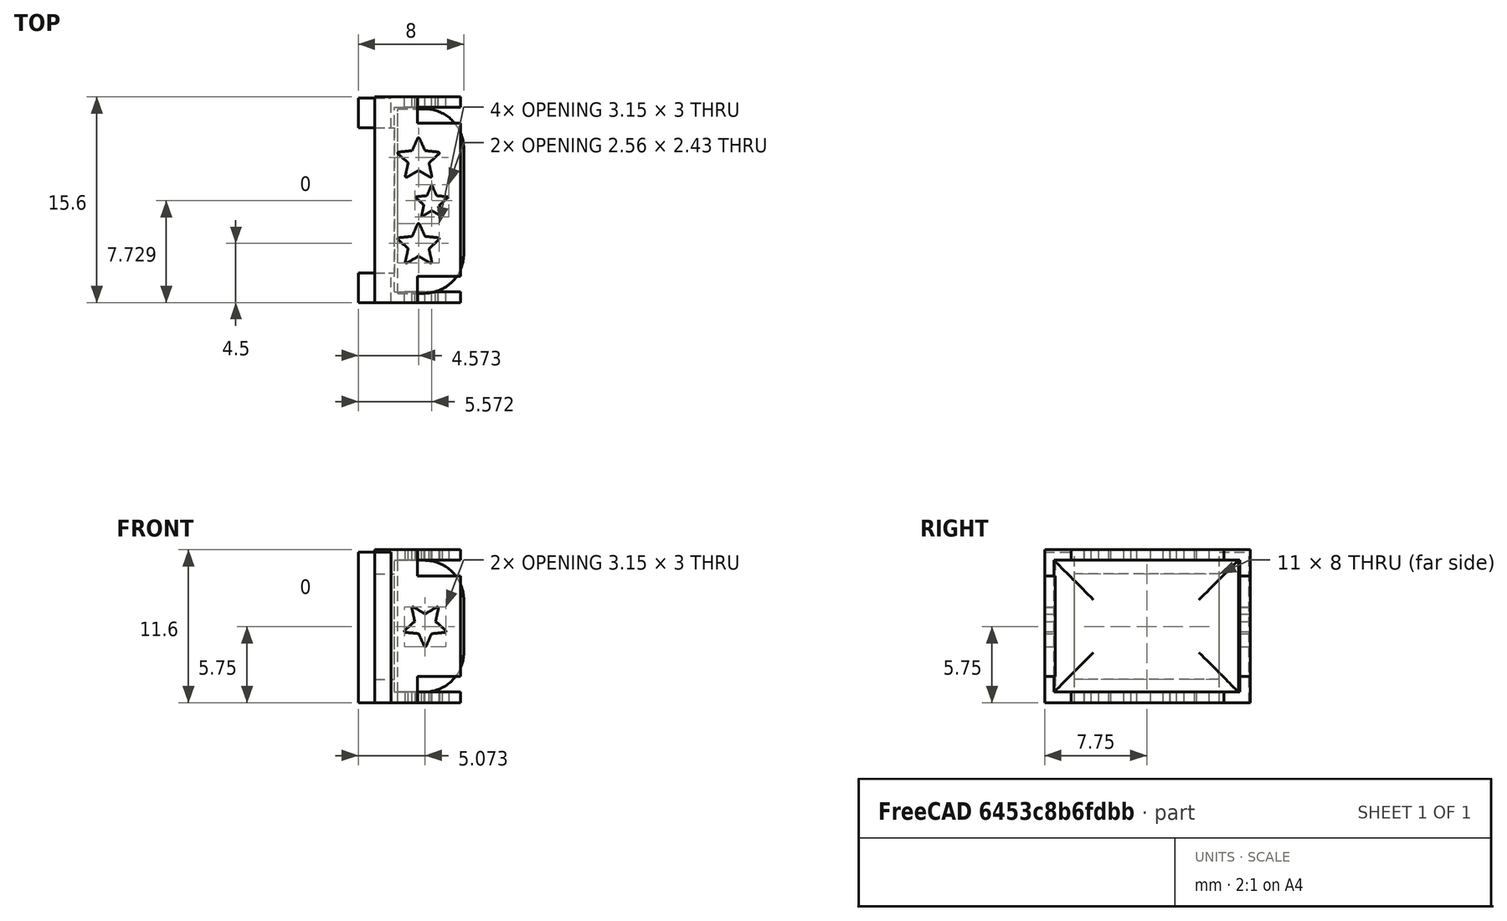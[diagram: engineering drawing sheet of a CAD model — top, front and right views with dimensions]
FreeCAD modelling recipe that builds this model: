
FCSTD DOCUMENT  (FreeCAD 0.19R)
Label: 14mmx10mm_rectangle_cabuchon
License: All rights reserved
LicenseURL: http://en.wikipedia.org/wiki/All_rights_reserved
objects: Part::Cut×11, Part::Box×10, Part::Feature×5, Part::Extrusion×5, Part::Fillet×1
note: 32 computed .brp shape members not serialized (recipe doc carries the construction recipe); baked Part::Feature solids carry a one-line shape summary decoded from their .brp

FEATURE [Part::Box] Box  label="Cube"
  AttacherType = Attacher::AttachEngine3D
  Height = 11.6
  Length = 6.5
  Placement = pos=(10.5,-7.5,-6.5) rot=(0,0,1;0rad)
  Width = 15.6
FEATURE [Part::Box] Box002  label="Cube002"
  AttacherType = Attacher::AttachEngine3D
  Height = 10
  Length = 5.75
  Placement = pos=(12,-6.7,-5.7) rot=(0,0,1;0rad)
  Width = 14
FEATURE [Part::Cut] Cut
  Base = -> Box
  Placement = pos=(1,0,0) rot=(0,0,1;0rad)
  Tool = -> Box002
FEATURE [Part::Box] Box004  label="Cube004"
  AttacherType = Attacher::AttachEngine3D
  Height = 8
  Length = 8
  Placement = pos=(11,-5.25,-4.75) rot=(0,0,1;0rad)
  Width = 11
FEATURE [Part::Cut] Cut001
  Base = -> Cut
  Placement = pos=(-1.25,0,0) rot=(0,0,1;0rad)
  Tool = -> Box004
FEATURE [Part::Box] Box006  label="Cube006"
  AttacherType = Attacher::AttachEngine3D
  Height = 11.4
  Length = 2.5
  Placement = pos=(9,-7.5,-6.5) rot=(0,0,1;0rad)
  Width = 2.25
FEATURE [Part::Box] Box007  label="Cube007"
  AttacherType = Attacher::AttachEngine3D
  Height = 11.4
  Length = 2.5
  Placement = pos=(9,5.75,-6.5) rot=(0,0,1;0rad)
  Width = 2.25
FEATURE [Part::Feature] path118
  shape: bbox 3.15 x 3.002 x 4.357e-07 mm, 0 faces, 0 solids (baked)
FEATURE [Part::Extrusion] Extrude
  Base = -> path118
  Dir = (0,0,1)
  DirMode = 2
  FaceMakerClass = Part::FaceMakerBullseye
  LengthFwd = 20
  LengthRev = 0
  Placement = pos=(19,1,-0.75) rot=(-1,0,0;1.5708rad)
  Solid = true
  Symmetric = false
FEATURE [Part::Feature] path119
  shape: bbox 3.15 x 3.002 x 4.357e-07 mm, 0 faces, 0 solids (baked)
FEATURE [Part::Extrusion] Extrude001
  Base = -> path119
  Dir = (0,0,1)
  DirMode = 2
  FaceMakerClass = Part::FaceMakerBullseye
  LengthFwd = 20
  LengthRev = 0
  Placement = pos=(12.5,-8,-2.25) rot=(-1,0,0;1.5708rad)
  Solid = true
  Symmetric = false
FEATURE [Part::Feature] path118001
  shape: bbox 3.15 x 3.002 x 4.357e-07 mm, 0 faces, 0 solids (baked)
FEATURE [Part::Feature] path118002
  shape: bbox 2.56 x 2.435 x 4.357e-07 mm, 0 faces, 0 solids (baked)
FEATURE [Part::Extrusion] Extrude002
  Base = -> path118001
  Dir = (0,0,1)
  DirMode = 2
  FaceMakerClass = Part::FaceMakerBullseye
  LengthFwd = 20
  LengthRev = 0
  Placement = pos=(12,5,-10) rot=(0,0,1;0rad)
  Solid = true
  Symmetric = false
FEATURE [Part::Extrusion] Extrude003
  Base = -> path118002
  Dir = (0,0,-1)
  DirMode = 2
  FaceMakerClass = Part::FaceMakerBullseye
  LengthFwd = 20
  LengthRev = 0
  Placement = pos=(13,1.75,7) rot=(0,0,1;0rad)
  Solid = true
  Symmetric = false
FEATURE [Part::Feature] path118003
  shape: bbox 3.15 x 3.002 x 4.357e-07 mm, 0 faces, 0 solids (baked)
FEATURE [Part::Extrusion] Extrude004
  Base = -> path118003
  Dir = (0,0,1)
  DirMode = 2
  FaceMakerClass = Part::FaceMakerBullseye
  LengthFwd = 20
  LengthRev = 0
  Placement = pos=(12,-1.5,-10) rot=(0,0,1;0rad)
  Solid = true
  Symmetric = false
FEATURE [Part::Cut] Cut002
  Base = -> Cut001
  Tool = -> Extrude001
FEATURE [Part::Cut] Cut003
  Base = -> Cut002
  Tool = -> Extrude004
FEATURE [Part::Cut] Cut004
  Base = -> Cut003
  Tool = -> Extrude
FEATURE [Part::Cut] Cut005
  Base = -> Cut004
  Tool = -> Extrude003
FEATURE [Part::Cut] Cut006
  Base = -> Cut005
  Tool = -> Extrude002
FEATURE [Part::Box] Box008  label="Cube008"
  AttacherType = Attacher::AttachEngine3D
  Height = 2
  Length = 4
  Placement = pos=(13.5,6.1,3.1) rot=(0,0,1;0rad)
  Width = 2
FEATURE [Part::Box] Box009  label="Cube009"
  AttacherType = Attacher::AttachEngine3D
  Height = 2
  Length = 4
  Placement = pos=(13.5,-7.5,3.1) rot=(0,0,1;0rad)
  Width = 2
FEATURE [Part::Box] Box010  label="Cube010"
  AttacherType = Attacher::AttachEngine3D
  Height = 2
  Length = 4
  Placement = pos=(13.5,-7.5,-6.5) rot=(0,0,1;0rad)
  Width = 2
FEATURE [Part::Box] Box011  label="Cube011"
  AttacherType = Attacher::AttachEngine3D
  Height = 2
  Length = 4
  Placement = pos=(13.5,6.1,-6.5) rot=(0,0,1;0rad)
  Width = 2
FEATURE [Part::Cut] Cut007
  Base = -> Cut006
  Tool = -> Box008
FEATURE [Part::Cut] Cut008
  Base = -> Cut007
  Tool = -> Box011
FEATURE [Part::Cut] Cut009
  Base = -> Cut008
  Tool = -> Box010
FEATURE [Part::Cut] Cut010  label="cabuchon_14x10mm"
  Base = -> Cut009
  Tool = -> Box009
FEATURE [Part::Box] Box012  label="Cube012"
  AttacherType = Attacher::AttachEngine3D
  Height = 10
  Length = 5
  Placement = pos=(12,-6.8,-5.7) rot=(0,0,1;0rad)
  Width = 14
FEATURE [Part::Fillet] Fillet  label="cabuchon_green"
  Base = -> Box012
  Edges = 4 edges r=3: [Edge5,Edge6,Edge7,Edge8]
